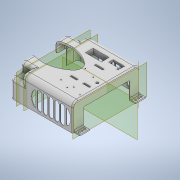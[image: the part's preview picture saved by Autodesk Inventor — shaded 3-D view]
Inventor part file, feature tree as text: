
AUTODESK INVENTOR PART (.ipt)
format: ipt  version: 2020 (Build 240168000, 168)  size: 1,312,768 bytes
history: native  units: in
note: dims shown in document units (in); Inventor stores cm internally (conversion verified against a paired STEP export)
features: extrude x25, projected_geometry x23, sketch x20, fillet x11, plane x8, mirror x4, thicken_offset x2, shell x1, pattern_linear x1, hole x1, other x1
ambient origin geometry x8: Origin, YZ Plane, XZ Plane, XY Plane, X Axis, Y Axis, Z Axis, Center Point
bodies: Solid1 (feature_tree)
feature tree (97):
  extrude  "Extrusion1"  Depth=3.189in
  shell  "Shell1"  Thickness=6.8701in
  thicken_offset  "Thicken1"
  thicken_offset  "Thicken2"
  extrude  "Extrusion3"  Depth=2.7559in TaperAngle=0.0deg
  extrude  "Extrusion4"  Depth=0.125in TaperAngle=0.0deg
  plane  "Work Plane1"
  mirror  "Mirror1"
  mirror  "Mirror2"
  extrude  "Extrusion8"  Depth=1.0in
  extrude  "Extrusion9"  Depth=0.1875in
  pattern_linear  "Rectangular Pattern2"  Count1=2 Spacing1=0.2756in
  mirror  "Mirror3"
  extrude  "Extrusion10"  Depth=0.125in
  fillet  "Fillet1"  Radius=4.1732in
  fillet  "Fillet2"  Radius=2.2904in
  extrude  "Extrusion11"  Depth=0.125in
  extrude  "Extrusion12"  Depth=0.125in
  fillet  "Fillet7"  Radius=1.1811in
  fillet  "Fillet8"  Radius=1.159in
  extrude  "Extrusion13"  Depth=0.125in TaperAngle=0.0deg
  extrude  "Extrusion32"  Depth=0.125in
  extrude  "Extrusion40"  Depth=0.125in
  hole  "Hole1"  [1 undecoded]
  plane  "Work Plane2"
  extrude  "Extrusion14"  Depth=0.125in
  plane  "Work Plane3"
  extrude  "Extrusion15"  Depth=0.125in
  plane  "Work Plane4"
  extrude  "Extrusion16"  Depth=0.3937in
  extrude  "Extrusion17"  Depth=0.125in TaperAngle=0.0deg
  fillet  "Fillet9"  Radius=0.9449in
  extrude  "Extrusion18"  Depth=0.125in TaperAngle=0.0deg
  plane  "Work Plane5"
  extrude  "Extrusion19"  Depth=0.125in
  fillet  "Fillet13"  Radius=0.5in
  plane  "Work Plane8"
  sketch  "Sketch23"  dims[d42=0.1875in]
  extrude  "Extrusion21"  Depth=0.125in
  mirror  "Mirror4"
  extrude  "Extrusion33"  Depth=0.125in
  extrude  "Extrusion34"  Depth=0.125in
  extrude  "Extrusion35"  Depth=0.125in
  extrude  "Extrusion36"  Depth=0.125in
  extrude  "Extrusion37"  Depth=0.125in
  extrude  "Extrusion38"  Depth=0.125in
  extrude  "Extrusion39"  Depth=0.125in
  fillet  "Fillet24"  Radius=0.1575in
  fillet  "Fillet25"  Radius=0.1575in
  fillet  "Fillet26"  Radius=0.857in
  fillet  "Fillet27"  Radius=0.5in
  fillet  "Fillet28"  Radius=0.1378in
  sketch  "Sketch1"  dims[d0=4.7244in d1=3.189in d2=6.8701in]
  sketch  "Sketch3"  dims[d4=5.3543in d5=2.7559in d6=0.0in]
  projected_geometry  "Projected Loop3"
  projected_geometry  "Projected Loop4"
  sketch  "Sketch9"  dims[d7=0.1969in d12=0.125in d13=0.0in]
  projected_geometry  "Projected Loop9"
  sketch  "Sketch10"  dims[d18=0.815in d19=1.0in]
  projected_geometry  "Projected Loop10"
  sketch  "Sketch11"  dims[d20=1.0in d21=0.1875in]
  projected_geometry  "Projected Loop11"
  sketch  "Sketch12"  dims[d22=0.1875in]
  projected_geometry  "Projected Loop12"
  sketch  "Sketch13"  dims[d23=0.1875in]
  projected_geometry  "Projected Loop13"
  projected_geometry  "Projected Loop14"
  sketch  "Sketch16"  dims[d24=0.125in d25=0.0in]
  projected_geometry  "Projected Loop15"
  projected_geometry  "Projected Loop16"
  sketch  "Sketch17"  dims[d40=1.0236in]
  projected_geometry  "Projected Loop17"
  projected_geometry  "Projected Loop18"
  projected_geometry  "Projected Loop19"
  sketch  "Sketch21"  dims[d41=0.1875in]
  other  "Work Axis1"
  plane  "Work Plane6"
  plane  "Work Plane7"
  projected_geometry  "Projected Loop22"
  sketch  "Sketch31"  dims[d43=0.1875in]
  sketch  "Sketch35"  dims[d44=0.815in]
  sketch  "Sketch36"  dims[d45=1.0in]
  projected_geometry  "Projected Loop43"
  sketch  "Sketch37"  dims[d46=1.0in]
  projected_geometry  "Projected Loop44"
  projected_geometry  "Projected Loop45"
  sketch  "Sketch38"  dims[d47=0.5236in]
  projected_geometry  "Projected Loop46"
  sketch  "Sketch39"  dims[d48=0.3937in d49=0.0in]
  projected_geometry  "Projected Loop47"
  sketch  "Sketch40"  dims[d50=0.1575in]
  projected_geometry  "Projected Loop48"
  projected_geometry  "Projected Loop49"
  sketch  "Sketch41"  dims[d51=0.3937in d52=0.0in d53=0.7874in d55=0.2756in]
  projected_geometry  "Projected Loop50"
  projected_geometry  "Projected Loop51"
  sketch  "Sketch42"  dims[d56=0.7874in d58=0.2756in d59=0.125in d60=4.1732in d61=2.2904in d62=1.7717in d63=2.1654in d64=1.1811in d66=1.159in d67=0.8661in d68=0.0in d69=0.1in d70=1.8898in d71=0.145in d72=0.45in d80=0.225in d81=1.9685in d83=0.59in d84=0.3937in d86=1.0in d88=1.0in d89=0.0in d90=0.9449in d91=1.0in d92=0.0in d107=0.68in d108=0.5in d109=0.1378in d110=0.1378in d111=0.1575in d112=0.1575in d114=0.68in d115=0.5in d120=0.1378in d121=0.1378in d122=0.1575in d123=0.1575in d128=0.857in d129=0.5in d130=0.1378in d131=0.1378in d132=0.1575in d133=0.1575in d135=0.2559in d137=1.5in d146=0.1988in d147=0.3209in d148=0.1575in d149=0.1378in d152=0.68in d153=0.1575in d154=1.1811in d155=0.68in d156=0.1575in d157=1.1811in d158=0.857in d159=0.1575in d160=1.1811in d161=1.0in d162=0.0in d163=0.4724in d164=0.4528in d165=1.1811in d166=0.15in d167=0.1575in d168=0.0831in d170=0.125in d171=0.125in d172=2.2in d173=0.0in d174=0.9843in d175=0.0in d177=1.1024in d178=1.1024in d179=0.0591in d180=0.0in d182=1.378in d183=0.5906in d184=0.0591in d185=0.0in d186=0.125in d188=2.9134in d190=1.6929in d191=1.5748in d192=1.3561in d193=0.3839in d194=1.3824in d195=1.0075in d196=1.2051in d198=0.0591in d199=0.0in d200=0.0591in d201=0.0in d205=0.1168in d208=0.125in d209=0.9843in d210=1.3386in d211=90.0deg d212=5.8046in d213=-0.7874in d214=1.2598in d215=0.9055in d216=0.9843in d217=0.0in d256=0.1378in d283=0.1378in d290=0.0689in d291=0.0689in d292=0.0689in d293=0.0689in d294=0.0689in d295=0.0689in d296=0.125in d297=0.0in d298=0.0968in d299=0.1in d300=0.375in d301=0.25in d302=0.5635in d303=0.346in d304=0.8108in d307=0.8661in d308=0.0in d309=0.0591in d310=0.0in d311=0.0591in d312=0.0in d313=0.0591in d314=0.0in d315=0.0591in d316=0.0in d317=0.7559in d318=5.8046in d319=0.854in d320=5.8046in d321=0.9843in d322=0.0in d323=0.5in d324=0.35in d325=0.049in d326=0.0in d327=0.35in d328=0.05in d329=0.125in d330=0.8in d331=1.65in d332=2.0in d333=1.0in d334=0.15in d335=0.375in d336=0.0in d337=0.1476in d338=0.1476in d339=0.1476in d340=0.1476in d10=0.5in d11=0.0344in d222=0.5in d223=0.0344in d224=0.5in d225=0.0344in]
note: 1 required parameter value undecoded (feature->parameter linkage not recoverable at this tier; creation-order binding heuristic only, values carry confidence <= 0.55)
